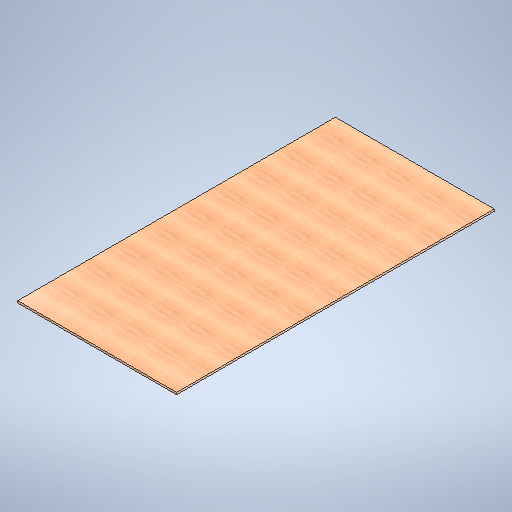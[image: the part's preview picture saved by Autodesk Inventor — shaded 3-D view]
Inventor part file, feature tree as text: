
AUTODESK INVENTOR PART (.ipt)
format: ipt  version: 2025 (Build 290162010, 162A)  size: 314,368 bytes
history: native  units: in
note: dims shown in document units (in); Inventor stores cm internally (conversion verified against a paired STEP export)
features: extrude x1, sketch x1
ambient origin geometry x8: Origin, YZ Plane, XZ Plane, XY Plane, X Axis, Y Axis, Z Axis, Center Point
bodies: Solid1 (feature_tree)
feature tree (2):
  extrude  "Extrusion1"  Depth=96.0in
  sketch  "Sketch1"  dims[d2=48.0in d3=96.0in d4=0.625in d5=0.0in]
